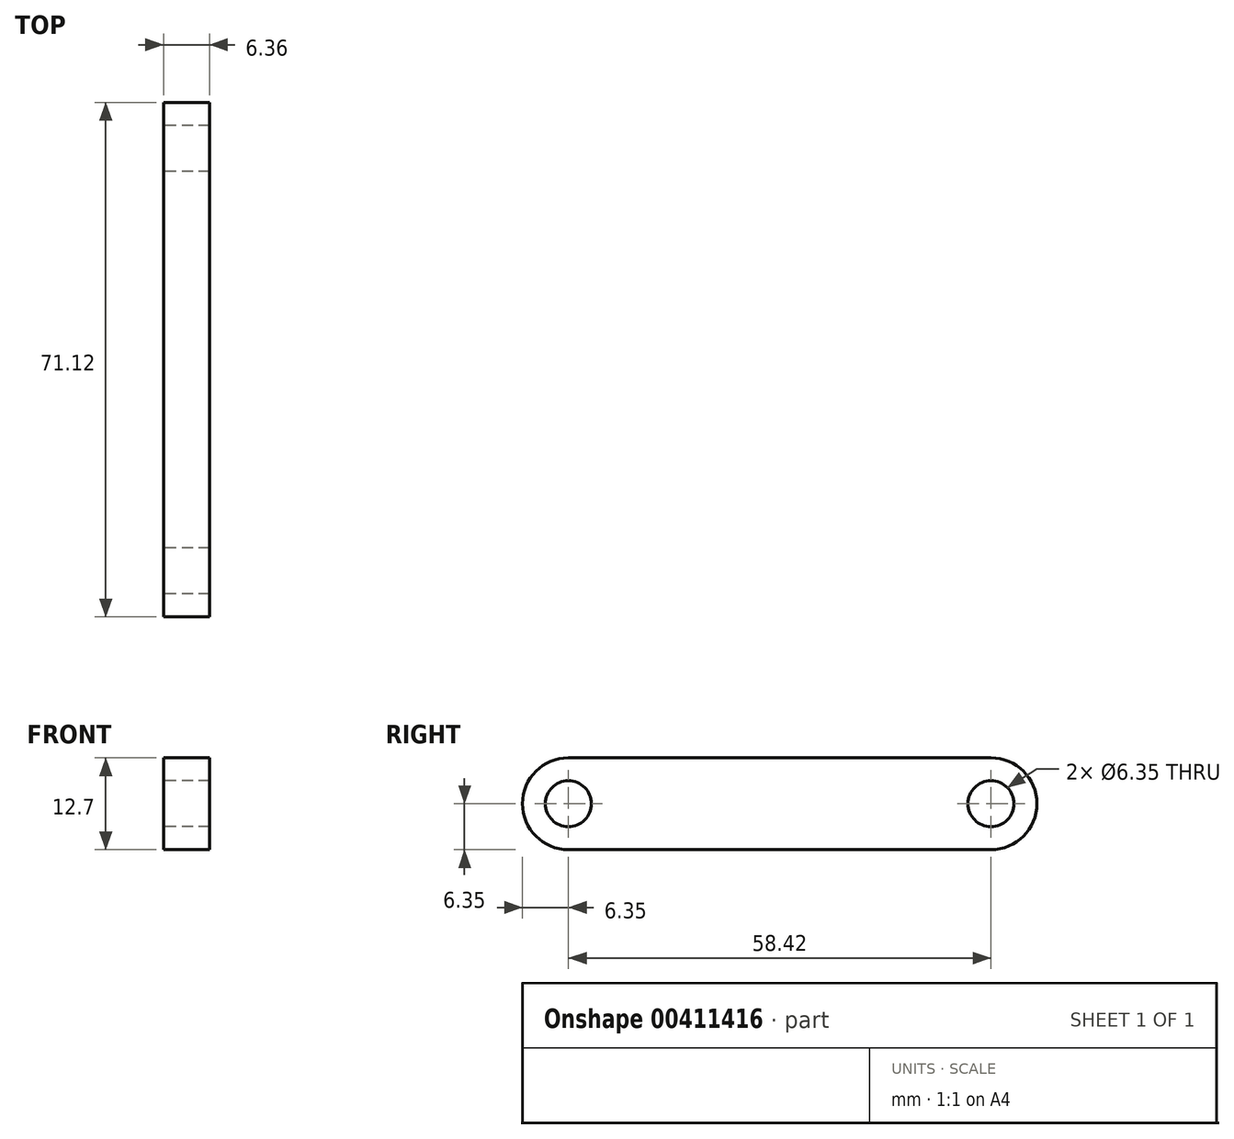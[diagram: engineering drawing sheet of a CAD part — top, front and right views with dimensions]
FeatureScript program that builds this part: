
annotation { "Feature Type Name" : "Feature", "Feature Type Description" : "" }
export const myFeature = defineFeature(function(context is Context, id is Id, definition is map)
    precondition{}
    {
        {
            var Q0;
            Q0=qCreatedBy(makeId("Right.planeOp"),FACE);
            var sketch = newSketch(context, id + "F0", { "sketchPlane" : qUnion([Q0])});
            skArc(sketch, "E0", {"start": v(0, 6.35) * mm, "mid": v(-6.35, 0) * mm, "end": v(0, -6.35) * mm});
            skArc(sketch, "E1", {"start": v(58.42, -6.35) * mm, "mid": v(64.77, 0) * mm, "end": v(58.42, 6.35) * mm});
            skLineSegment(sketch, "E2", {"start": v(0, 6.35) * mm, "end": v(58.42, 6.35) * mm});
            skLineSegment(sketch, "E3", {"start": v(0, -6.35) * mm, "end": v(58.42, -6.35) * mm});
            skCircle(sketch, "E4", {"center": v(0, 0) * mm, "radius": 3.18 * mm});
            skCircle(sketch, "E5", {"center": v(58.42, 0) * mm, "radius": 3.18 * mm});
            skSolve(sketch);
        }
        {
            var Q0;
            Q0 = qSketchRegion(id + "F0", true);
            extrude(context, id + "F1", {"entities" : qUnion([Q0]), "endBound" : BoundingType.SYMMETRIC, "depth" : 6.35 * mm});
        }
    });
